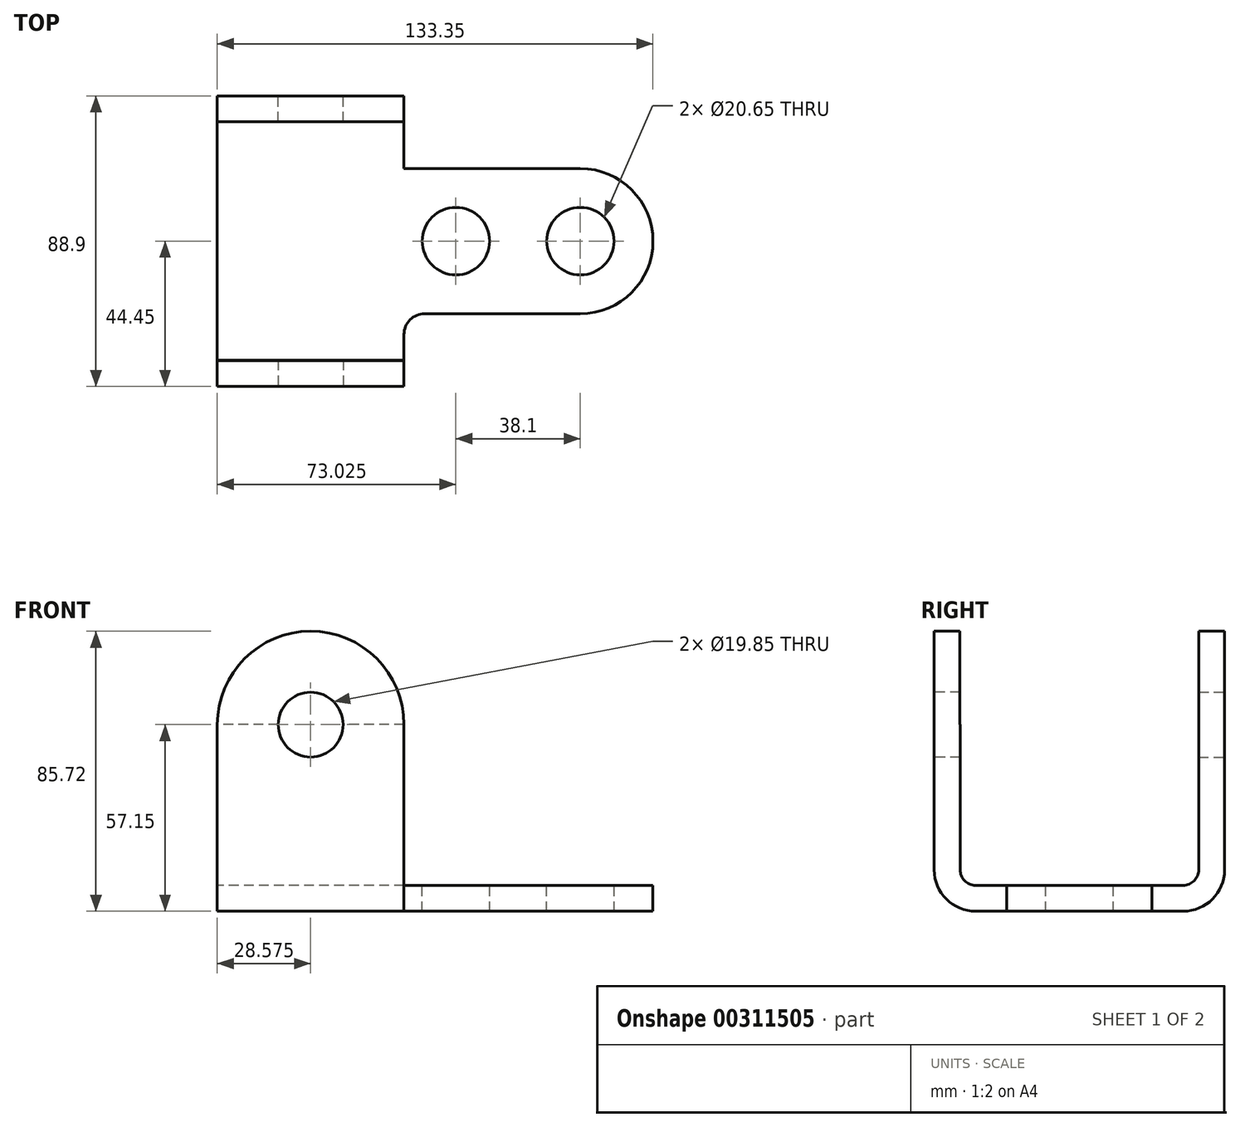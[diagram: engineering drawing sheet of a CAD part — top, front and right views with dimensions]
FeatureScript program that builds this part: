
annotation { "Feature Type Name" : "Feature", "Feature Type Description" : "" }
export const myFeature = defineFeature(function(context is Context, id is Id, definition is map)
    precondition{}
    {
        {
            var Q0;
            Q0=qCreatedBy(makeId("Right.planeOp"),FACE);
            var sketch = newSketch(context, id + "F0", { "sketchPlane" : qUnion([Q0])});
            skLineSegment(sketch, "E0", {"start": v(0, 0) * mm, "end": v(63.5, 0) * mm});
            skArc(sketch, "E1", {"start": v(63.5, 0) * mm, "mid": v(72.48, 3.72) * mm, "end": v(76.2, 12.7) * mm});
            skArc(sketch, "E2", {"start": v(-12.7, 12.7) * mm, "mid": v(-8.98, 3.72) * mm, "end": v(0, 0) * mm});
            skLineSegment(sketch, "E3", {"start": v(76.2, 12.7) * mm, "end": v(76.2, 57.15) * mm});
            skLineSegment(sketch, "E4", {"start": v(-12.7, 12.7) * mm, "end": v(-12.7, 57.15) * mm});
            skLineSegment(sketch, "E5", {"start": v(76.2, 57.15) * mm, "end": v(68.26, 57.15) * mm});
            skLineSegment(sketch, "E6", {"start": v(68.26, 57.15) * mm, "end": v(68.26, 12.7) * mm});
            skLineSegment(sketch, "E7", {"start": v(-12.7, 57.15) * mm, "end": v(-4.76, 57.15) * mm});
            skLineSegment(sketch, "E8", {"start": v(-4.76, 57.15) * mm, "end": v(-4.76, 12.7) * mm});
            skArc(sketch, "E9", {"start": v(-4.76, 12.7) * mm, "mid": v(-3.37, 9.33) * mm, "end": v(0, 7.94) * mm});
            skArc(sketch, "E10", {"start": v(63.5, 7.94) * mm, "mid": v(66.87, 9.33) * mm, "end": v(68.26, 12.7) * mm});
            skLineSegment(sketch, "E11", {"start": v(63.5, 7.94) * mm, "end": v(0, 7.94) * mm});
            skSolve(sketch);
        }
        {
            var Q0;
            Q0 = qSketchRegion(id + "F0", true);
            extrude(context, id + "F1", {"entities" : qUnion([Q0]), "depth" : 57.15 * mm});
        }
        {
            var Q0;
            Q0=makeQuery(id+"F1.opExtrude","SWEPT_FACE",FACE,{"disambiguationData":[OSD([sQuery(id+"F0.wireOp",EDGE,"E4")])]});
            var sketch = newSketch(context, id + "F2", { "sketchPlane" : qUnion([Q0])});
            skArc(sketch, "E12", {"start": v(57.15, 57.15) * mm, "mid": v(28.58, 85.73) * mm, "end": v(0, 57.15) * mm});
            skLineSegment(sketch, "E13", {"start": v(57.15, 57.15) * mm, "end": v(0, 57.15) * mm});
            skSolve(sketch);
        }
        {
            var Q0;
            Q0 = qSketchRegion(id + "F2", true);
            extrude(context, id + "F3", {"entities" : qUnion([Q0]), "operationType" : NewBodyOperationType.ADD, "oppositeDirection" : true, "depth" : 7.87 * mm});
        }
        {
            var Q0;
            Q0=makeQuery(id+"F1.opExtrude","SWEPT_FACE",FACE,{"disambiguationData":[OSD([sQuery(id+"F0.wireOp",EDGE,"E3")])]});
            var sketch = newSketch(context, id + "F4", { "sketchPlane" : qUnion([Q0])});
            skArc(sketch, "E14", {"start": v(0, 57.15) * mm, "mid": v(-28.57, 85.73) * mm, "end": v(-57.15, 57.15) * mm});
            skLineSegment(sketch, "E15", {"start": v(0, 57.15) * mm, "end": v(-57.15, 57.15) * mm});
            skSolve(sketch);
        }
        {
            var Q0;
            Q0 = qSketchRegion(id + "F4", true);
            extrude(context, id + "F5", {"entities" : qUnion([Q0]), "operationType" : NewBodyOperationType.ADD, "oppositeDirection" : true, "depth" : 7.87 * mm});
        }
        {
            var Q0;
            Q0=makeQuery(id+"F3.boolean.opBoolean","MERGE",FACE,{"derivedFrom":[makeQuery(id+"F1.opExtrude","SWEPT_FACE",FACE,{"disambiguationData":[OSD([sQuery(id+"F0.wireOp",EDGE,"E4")])]}),makeQuery(id+"F3.opExtrude","CAP_FACE",FACE,{"disambiguationData":[OSD([sQuery(id+"F2.wireOp",EDGE,"E12"),sQuery(id+"F2.wireOp",EDGE,"E13")])],"isStart":true})]});
            var sketch = newSketch(context, id + "F6", { "sketchPlane" : qUnion([Q0])});
            skCircle(sketch, "E16", {"center": v(28.58, 57.15) * mm, "radius": 9.92 * mm});
            skSolve(sketch);
        }
        {
            var Q0;
            Q0 = qSketchRegion(id + "F6", true);
            extrude(context, id + "F7", {"entities" : qUnion([Q0]), "operationType" : NewBodyOperationType.REMOVE, "oppositeDirection" : true, "depth" : 25.4 * mm});
        }
        {
            var Q0;
            Q0=makeQuery(id+"F5.boolean.opBoolean","MERGE",FACE,{"derivedFrom":[makeQuery(id+"F1.opExtrude","SWEPT_FACE",FACE,{"disambiguationData":[OSD([sQuery(id+"F0.wireOp",EDGE,"E3")])]}),makeQuery(id+"F5.opExtrude","CAP_FACE",FACE,{"disambiguationData":[OSD([sQuery(id+"F4.wireOp",EDGE,"E14"),sQuery(id+"F4.wireOp",EDGE,"E15")])],"isStart":true})]});
            var sketch = newSketch(context, id + "F8", { "sketchPlane" : qUnion([Q0])});
            skCircle(sketch, "E17", {"center": v(-28.58, 57.15) * mm, "radius": 9.92 * mm});
            skSolve(sketch);
        }
        {
            var Q0;
            Q0 = qSketchRegion(id + "F8", true);
            extrude(context, id + "F9", {"entities" : qUnion([Q0]), "operationType" : NewBodyOperationType.REMOVE, "oppositeDirection" : true, "depth" : 25.4 * mm});
        }
        {
            var Q0;
            Q0=makeQuery(id+"F1.opExtrude","SWEPT_FACE",FACE,{"disambiguationData":[OSD([sQuery(id+"F0.wireOp",EDGE,"E11")])]});
            var sketch = newSketch(context, id + "F10", { "sketchPlane" : qUnion([Q0])});
            skLineSegment(sketch, "E18", {"start": v(57.15, 9.52) * mm, "end": v(57.15, 53.98) * mm});
            skPoint(sketch, "E19", {"position": v(57.15, 31.75) * mm});
            skLineSegment(sketch, "E20", {"start": v(57.15, 53.98) * mm, "end": v(133.35, 53.98) * mm});
            skLineSegment(sketch, "E21", {"start": v(57.15, 9.52) * mm, "end": v(133.35, 9.52) * mm});
            skLineSegment(sketch, "E22", {"start": v(133.35, 9.52) * mm, "end": v(133.35, 53.98) * mm});
            skSolve(sketch);
        }
        {
            var Q0;
            Q0 = qSketchRegion(id + "F10", true);
            extrude(context, id + "F11", {"entities" : qUnion([Q0]), "operationType" : NewBodyOperationType.ADD, "oppositeDirection" : true, "depth" : 7.94 * mm});
        }
        {
            var Q0;
            Q0=makeQuery(id+"F11.boolean.opBoolean","MERGE",FACE,{"derivedFrom":[makeQuery(id+"F1.opExtrude","SWEPT_FACE",FACE,{"disambiguationData":[OSD([sQuery(id+"F0.wireOp",EDGE,"E11")])]}),makeQuery(id+"F11.opExtrude","CAP_FACE",FACE,{"disambiguationData":[OSD([sQuery(id+"F10.wireOp",EDGE,"E18"),sQuery(id+"F10.wireOp",EDGE,"E20"),sQuery(id+"F10.wireOp",EDGE,"E21"),sQuery(id+"F10.wireOp",EDGE,"E22")])],"isStart":true})]});
            var sketch = newSketch(context, id + "F12", { "sketchPlane" : qUnion([Q0])});
            skCircle(sketch, "E23", {"center": v(73.03, 31.75) * mm, "radius": 10.33 * mm});
            skPoint(sketch, "E23.centerSnap0", {"position": v(133.35, 31.75) * mm});
            skCircle(sketch, "E24", {"center": v(111.12, 31.75) * mm, "radius": 10.33 * mm});
            skCircle(sketch, "E25", {"center": v(111.12, 31.75) * mm, "radius": 22.23 * mm});
            skSolve(sketch);
        }
        {
            var Q0;
            Q0=makeQuery(id+"F12.imprint","IMPRINT",FACE,{"disambiguationData":[TD([[makeQuery(id+"F12.imprint","IMPRINT",EDGE,{"derivedFrom":sQuery(id+"F12.wireOp",EDGE,"E23")}),1.0]])]});
            var Q1;
            Q1=makeQuery(id+"F12.imprint","IMPRINT",FACE,{"disambiguationData":[TD([[makeQuery(id+"F12.imprint","IMPRINT",EDGE,{"derivedFrom":sQuery(id+"F12.wireOp",EDGE,"E24")}),1.0]])]});
            var Q2;
            {var subQ0=sQuery(id+"F12.wireOp",EDGE,"E25");var subQ1=makeQuery(id+"F11.opExtrude","CAP_EDGE",EDGE,{"disambiguationData":[OSD([sQuery(id+"F10.wireOp",EDGE,"E20")])],"isStart":true});var subQ2=makeQuery(id+"F12.imprint","INTERSECT",VERTEX,{"derivedFrom":[subQ1,subQ0]});Q2=makeQuery(id+"F12.imprint","IMPRINT",FACE,{"disambiguationData":[TD([[makeQuery(id+"F12.imprint","IMPRINT",EDGE,{"disambiguationData":[TD([[subQ2,1.0]])],"derivedFrom":subQ0}),-1.0]])]});}
            var Q3;
            {var subQ0=sQuery(id+"F12.wireOp",EDGE,"E25");var subQ1=makeQuery(id+"F11.opExtrude","CAP_EDGE",EDGE,{"disambiguationData":[OSD([sQuery(id+"F10.wireOp",EDGE,"E22")])],"isStart":true});var subQ2=makeQuery(id+"F12.imprint","INTERSECT",VERTEX,{"derivedFrom":[subQ1,subQ0]});Q3=makeQuery(id+"F12.imprint","IMPRINT",FACE,{"disambiguationData":[TD([[makeQuery(id+"F12.imprint","IMPRINT",EDGE,{"disambiguationData":[TD([[subQ2,1.0]])],"derivedFrom":subQ0}),-1.0]])]});}
            extrude(context, id + "F13", {"entities" : qUnion([Q0, Q1, Q2, Q3]), "operationType" : NewBodyOperationType.REMOVE, "oppositeDirection" : true, "depth" : 25.4 * mm});
        }
        {
            var Q0;
            Q0=makeQuery(id+"F11.opExtrude","SWEPT_EDGE",EDGE,{"disambiguationData":[OSD([sQuery(id+"F0.wireOp",EDGE,"E11"),sQuery(id+"F10.wireOp",EDGE,"E18"),sQuery(id+"F10.wireOp",EDGE,"E21")])]});
            var Q1;
            Q1=makeQuery(id+"F11.opExtrude","SWEPT_EDGE",EDGE,{"disambiguationData":[OSD([sQuery(id+"F0.wireOp",EDGE,"E11"),sQuery(id+"F10.wireOp",EDGE,"E18"),sQuery(id+"F10.wireOp",EDGE,"E20")])]});
            fillet(context, id + "F14", {"entities" : qUnion([Q0, Q1]), "radius" : 6.35 * mm, "tangentPropagation" : true, "allowEdgeOverflow" : false});
        }
    });
